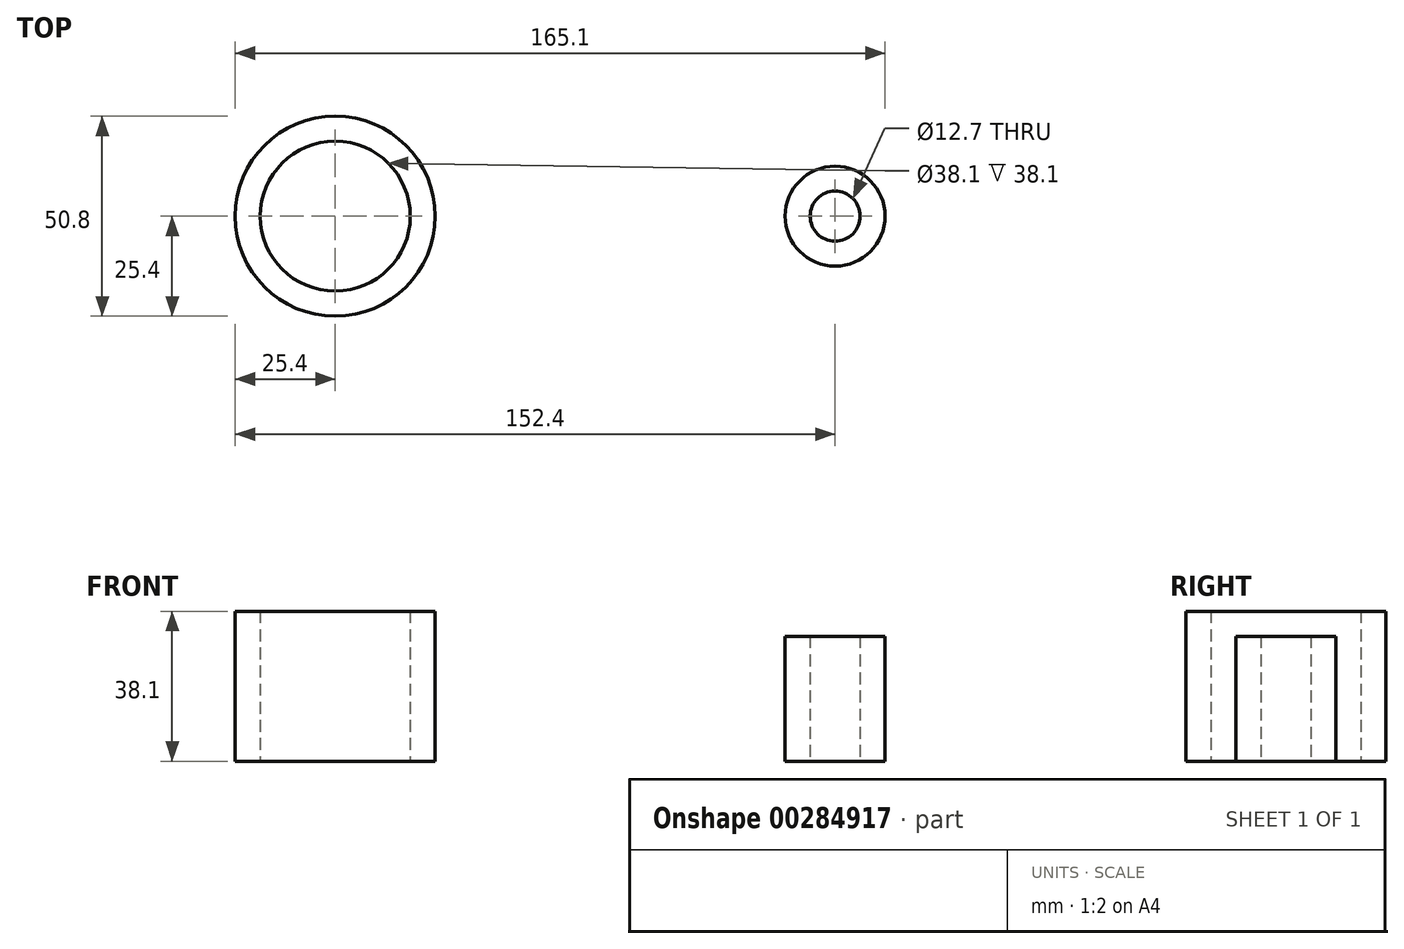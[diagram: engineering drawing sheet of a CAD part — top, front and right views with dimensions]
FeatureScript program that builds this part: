
annotation { "Feature Type Name" : "Feature", "Feature Type Description" : "" }
export const myFeature = defineFeature(function(context is Context, id is Id, definition is map)
    precondition{}
    {
        {
            var Q0;
            Q0=qCreatedBy(makeId("Top.planeOp"),FACE);
            var sketch = newSketch(context, id + "F0", { "sketchPlane" : qUnion([Q0])});
            skCircle(sketch, "E0", {"center": v(-88.9, 0) * mm, "radius": 25.4 * mm});
            skCircle(sketch, "E1", {"center": v(38.1, 0) * mm, "radius": 12.7 * mm});
            skCircle(sketch, "E2", {"center": v(-88.9, 0) * mm, "radius": 19.05 * mm});
            skCircle(sketch, "E3", {"center": v(38.1, 0) * mm, "radius": 6.35 * mm});
            skLineSegment(sketch, "E4", {"start": v(-86.36, 25.27) * mm, "end": v(39.37, 12.64) * mm});
            skLineSegment(sketch, "E5", {"start": v(-86.36, -25.27) * mm, "end": v(38.35, -12.74) * mm});
            skCircle(sketch, "E6", {"center": v(-50.8, 0) * mm, "radius": 6.35 * mm});
            skCircle(sketch, "E7", {"center": v(0, 0) * mm, "radius": 6.35 * mm});
            skLineSegment(sketch, "E8", {"start": v(-50.8, 6.35) * mm, "end": v(0, 6.35) * mm});
            skLineSegment(sketch, "E9", {"start": v(-50.8, -6.35) * mm, "end": v(0, -6.35) * mm});
            skSolve(sketch);
        }
        {
            var Q0;
            Q0=makeQuery(id+"F0.imprint","IMPRINT",FACE,{"disambiguationData":[TD([[makeQuery(id+"F0.imprint","IMPRINT",EDGE,{"derivedFrom":sQuery(id+"F0.wireOp",EDGE,"E2")}),-1.0]])]});
            extrude(context, id + "F1", {"entities" : qUnion([Q0]), "depth" : 38.1 * mm});
        }
        {
            var Q0;
            Q0=makeQuery(id+"F0.imprint","IMPRINT",FACE,{"disambiguationData":[TD([[makeQuery(id+"F0.imprint","IMPRINT",EDGE,{"derivedFrom":sQuery(id+"F0.wireOp",EDGE,"E1")}),1.0]])]});
            extrude(context, id + "F2", {"entities" : qUnion([Q0]), "depth" : 31.75 * mm});
        }
    });
